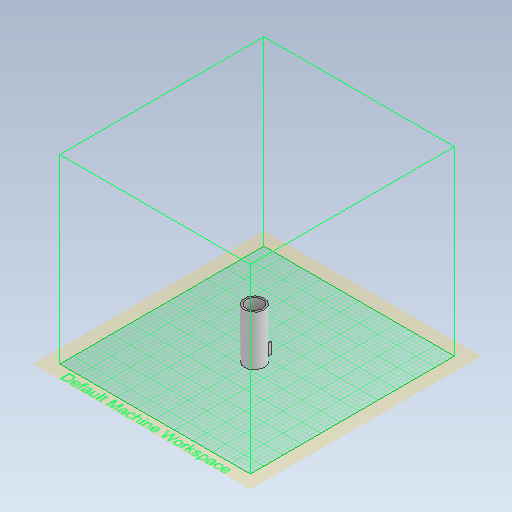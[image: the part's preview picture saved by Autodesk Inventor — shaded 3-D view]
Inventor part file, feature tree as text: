
AUTODESK INVENTOR PART (.ipt)
format: ipt  version: 2021 (Build 250183000, 183)  size: 499,200 bytes
history: native  units: in
note: dims shown in document units (in); Inventor stores cm internally (conversion verified against a paired STEP export)
features: projected_geometry x11, extrude x9, sketch x5, chamfer x3, plane x1, pattern_linear x1, fillet x1
ambient origin geometry x8: Origin, YZ Plane, XZ Plane, XY Plane, X Axis, Y Axis, Z Axis, Center Point
bodies: Solid1 (feature_tree)
feature tree (31):
  extrude  "Extrusion1"  Depth=4.3307in TaperAngle=0.0deg
  plane  "Work Plane1"
  extrude  "Extrusion7"  Depth=4.252in TaperAngle=0.0deg
  extrude  "Extrusion8"  Depth=0.2756in
  extrude  "Extrusion9"  Depth=0.2047in
  extrude  "Extrusion10"  Depth=0.0295in TaperAngle=0.0deg
  extrude  "Extrusion11"  Depth=0.0591in
  extrude  "Extrusion12"  Depth=0.0591in
  pattern_linear  "Rectangular Pattern3"  Spacing1=0.1969in  [1 undecoded]
  extrude  "Extrusion13"  Depth=1.1811in TaperAngle=0.0deg
  chamfer  "Chamfer2"  Distance=1.811in
  chamfer  "Chamfer4"  Distance=0.0394in
  chamfer  "Chamfer5"  Distance=0.0098in
  extrude  "Extrusion14"  Depth=8.2677in
  fillet  "Fillet11"  Radius=0.1181in
  sketch  "Sketch2"  dims[d2=1.752in d3=4.3307in d4=0.0in]
  sketch  "Sketch9"  dims[d54=1.4173in d55=4.252in d56=0.0in]
  projected_geometry  "Projected Loop7"
  sketch  "Sketch10"  dims[d57=0.3937in d58=0.2756in]
  projected_geometry  "Projected Loop8"
  projected_geometry  "Projected Loop9"
  projected_geometry  "Projected Loop10"
  projected_geometry  "Projected Loop11"
  projected_geometry  "Projected Loop12"
  projected_geometry  "Projected Loop14"
  projected_geometry  "Projected Loop15"
  sketch  "Sketch16"  dims[d59=0.3937in d60=0.0236in d61=0.0in d62=0.0in d63=0.2047in]
  projected_geometry  "Projected Loop16"
  sketch  "Sketch17"  dims[d64=0.126in d66=0.0295in d67=0.0in d68=0.0591in d69=0.0591in d71=0.1969in d72=0.0in d76=1.1811in d77=0.0in d84=1.811in d85=0.0394in d86=0.0098in d87=0.0in d88=8.2677in d90=0.0787in d92=0.1181in d93=0.3937in d94=0.0in d96=0.0059in d97=0.0185in d98=0.0787in d99=45.0deg d103=0.1575in d104=0.0787in d105=45.0deg d106=0.0098in d107=0.0787in d108=45.0deg d109=0.2756in d110=0.0315in d111=0.0in d116=0.4724in d19=0.0197in d20=0.0344in d21=0.0197in d22=0.0344in]
  projected_geometry  "Projected Loop17"
  projected_geometry  "Projected Loop18"
note: 1 required parameter value undecoded (feature->parameter linkage not recoverable at this tier; creation-order binding heuristic only, values carry confidence <= 0.55)
